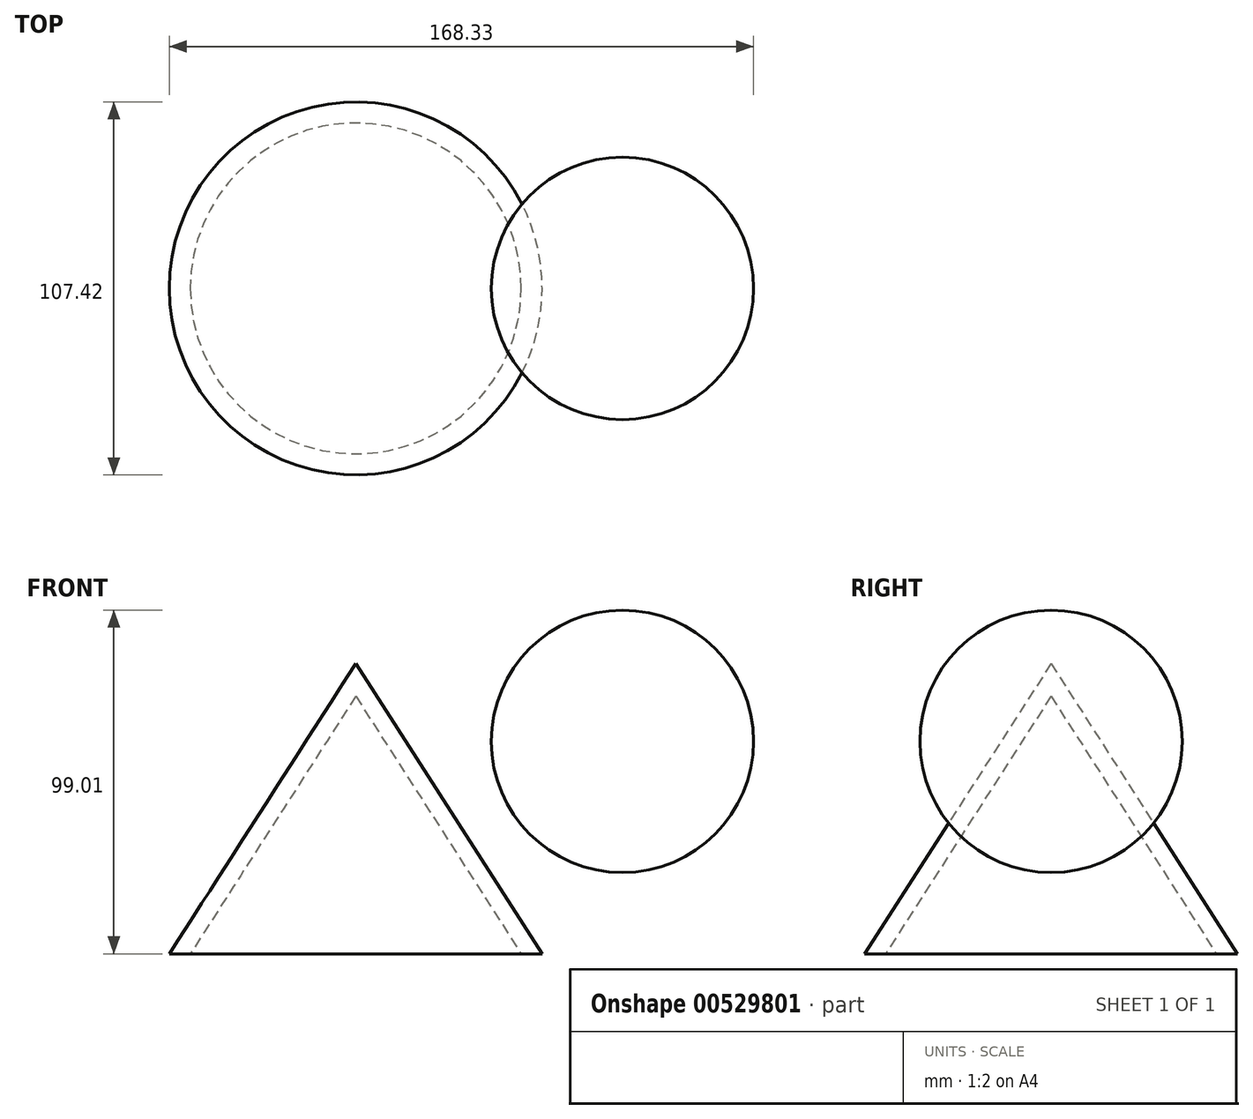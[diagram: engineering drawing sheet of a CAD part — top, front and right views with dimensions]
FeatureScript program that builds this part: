
annotation { "Feature Type Name" : "Feature", "Feature Type Description" : "" }
export const myFeature = defineFeature(function(context is Context, id is Id, definition is map)
    precondition{}
    {
        {
            var Q0;
            Q0=qCreatedBy(makeId("Front.planeOp"),FACE);
            var sketch = newSketch(context, id + "F0", { "sketchPlane" : qUnion([Q0])});
            skLineSegment(sketch, "E0", {"start": v(-17.67, 0) * mm, "end": v(57.9, 0) * mm});
            skArc(sketch, "E1", {"start": v(57.9, 0) * mm, "mid": v(20.12, 37.79) * mm, "end": v(-17.67, 0) * mm});
            skSolve(sketch);
        }
        {
            var Q0;
            Q0=makeQuery(id+"F0.imprint","IMPRINT",FACE,{"disambiguationData":[TD([[makeQuery(id+"F0.imprint","IMPRINT",EDGE,{"derivedFrom":sQuery(id+"F0.wireOp",EDGE,"E0")}),1.0]])]});
            var Q1;
            Q1=sQuery(id+"F0.wireOp",EDGE,"E0");
            revolve(context, id + "F1", {"entities" : qUnion([Q0]), "axis" : qUnion([Q1]), "revolveType" : RevolveType.FULL});
        }
        {
            var Q0;
            Q0=qCreatedBy(makeId("Front.planeOp"),FACE);
            var sketch = newSketch(context, id + "F2", { "sketchPlane" : qUnion([Q0])});
            skLineSegment(sketch, "E2", {"start": v(-56.72, -61.22) * mm, "end": v(-56.72, 22.4) * mm});
            skLineSegment(sketch, "E3", {"start": v(-110.43, -61.22) * mm, "end": v(-56.72, -61.22) * mm});
            skLineSegment(sketch, "E4", {"start": v(-110.43, -61.22) * mm, "end": v(-56.72, 22.4) * mm});
            skSolve(sketch);
        }
        {
            var Q0;
            Q0=makeQuery(id+"F2.imprint","IMPRINT",FACE,{"disambiguationData":[TD([[makeQuery(id+"F2.imprint","IMPRINT",EDGE,{"derivedFrom":sQuery(id+"F2.wireOp",EDGE,"E2")}),1.0]])]});
            var Q1;
            Q1=sQuery(id+"F2.wireOp",EDGE,"E2");
            revolve(context, id + "F3", {"entities" : qUnion([Q0]), "axis" : qUnion([Q1]), "revolveType" : RevolveType.FULL});
        }
        {
            var Q0;
            Q0=makeQuery(id+"F3.opRevolve","SWEPT_FACE",FACE,{"disambiguationData":[OSD([sQuery(id+"F2.wireOp",EDGE,"E3")])]});
            shell(context, id + "F4", {"entities" : qUnion([Q0]), "thickness" : 5.08 * mm});
        }
    });
